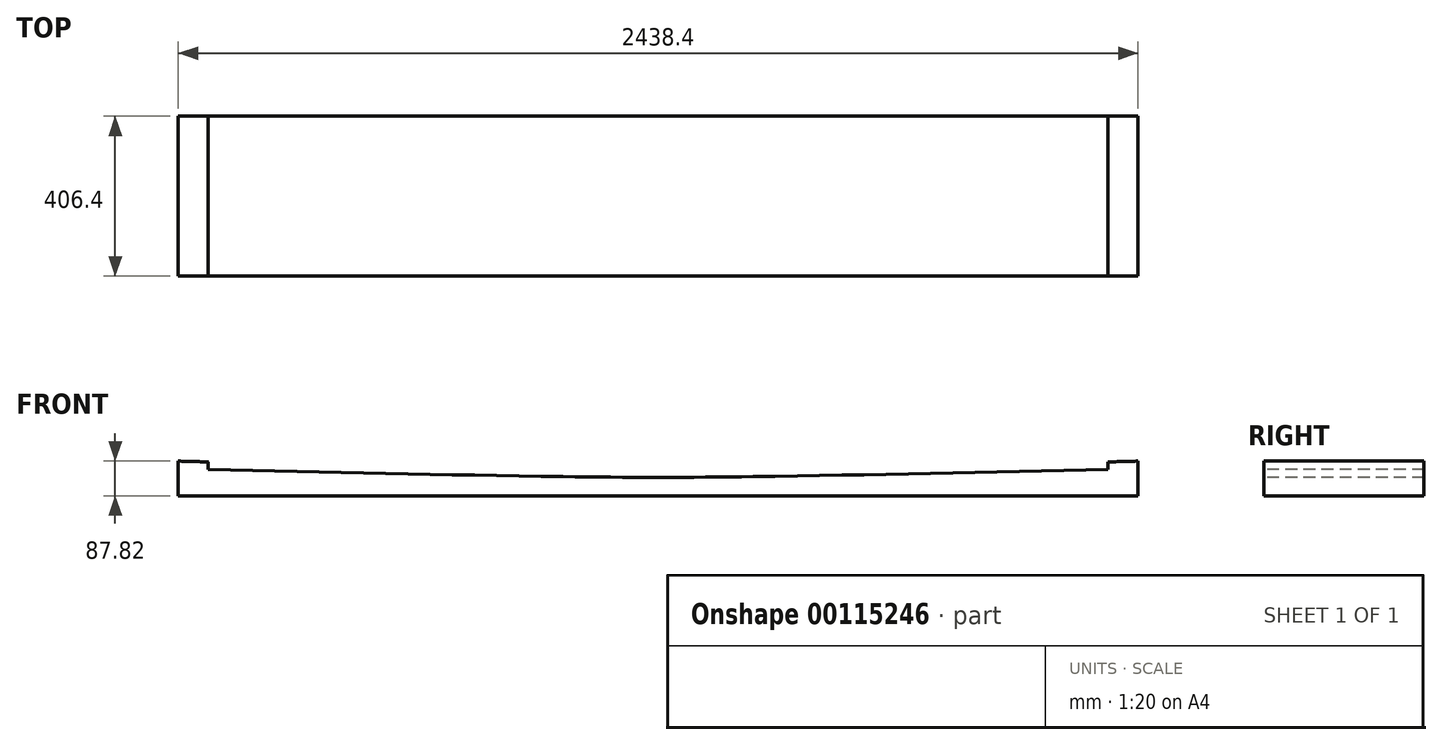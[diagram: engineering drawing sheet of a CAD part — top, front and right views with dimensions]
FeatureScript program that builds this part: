
annotation { "Feature Type Name" : "Feature", "Feature Type Description" : "" }
export const myFeature = defineFeature(function(context is Context, id is Id, definition is map)
    precondition{}
    {
        {
            var Q0;
            Q0=qCreatedBy(makeId("Front.planeOp"),FACE);
            var sketch = newSketch(context, id + "F0", { "sketchPlane" : qUnion([Q0])});
            skLineSegment(sketch, "E0", {"start": v(0, 0) * mm, "end": v(2438.4, 0) * mm});
            skLineSegment(sketch, "E1", {"start": v(1219.2, 0) * mm, "end": v(1219.2, 46.56) * mm, "construction": true});
            skArc(sketch, "E2", {"start": v(1219.2, 46.56) * mm, "mid": v(1098.4, 47.04) * mm, "end": v(977.6, 48.48) * mm});
            skLineSegment(sketch, "E3", {"start": v(977.6, 48.48) * mm, "end": v(977.6, 0) * mm, "construction": true});
            skLineSegment(sketch, "E4", {"start": v(76.2, 66.83) * mm, "end": v(76.2, 85.9) * mm});
            skArc(sketch, "E5.MirrorCS", {"start": v(1219.2, 46.56) * mm, "mid": v(1340, 47.04) * mm, "end": v(1460.8, 48.48) * mm});
            skLineSegment(sketch, "E6.MirrorCS", {"start": v(2362.2, 66.83) * mm, "end": v(2362.2, 85.9) * mm});
            skArc(sketch, "E7", {"start": v(977.6, 48.48) * mm, "mid": v(526.88, 56.64) * mm, "end": v(76.2, 66.83) * mm});
            skArc(sketch, "E8.MirrorCS", {"start": v(1460.8, 48.48) * mm, "mid": v(1911.52, 56.64) * mm, "end": v(2362.2, 66.83) * mm});
            skArc(sketch, "E9.0", {"start": v(2362.2, 85.9) * mm, "mid": v(2400.06, 86.84) * mm, "end": v(2437.91, 87.8) * mm});
            skArc(sketch, "E10.extension", {"start": v(2437.91, 87.8) * mm, "mid": v(2438.16, 87.8) * mm, "end": v(2438.4, 87.82) * mm});
            skArc(sketch, "E11.extension", {"start": v(76.2, 85.9) * mm, "mid": v(38.1, 86.85) * mm, "end": v(0, 87.82) * mm});
            skLineSegment(sketch, "E12", {"start": v(2438.4, 0) * mm, "end": v(2438.4, 87.82) * mm});
            skLineSegment(sketch, "E13", {"start": v(0, 0) * mm, "end": v(0, 87.82) * mm});
            skSolve(sketch);
        }
        {
            var Q0;
            Q0=makeQuery(id+"F0.imprint","IMPRINT",FACE,{"disambiguationData":[TD([[makeQuery(id+"F0.imprint","IMPRINT",EDGE,{"derivedFrom":sQuery(id+"F0.wireOp",EDGE,"E0")}),1.0]])]});
            extrude(context, id + "F1", {"entities" : qUnion([Q0]), "oppositeDirection" : true, "depth" : 406.4 * mm, "offsetDistance" : 25 * mm});
        }
    });
